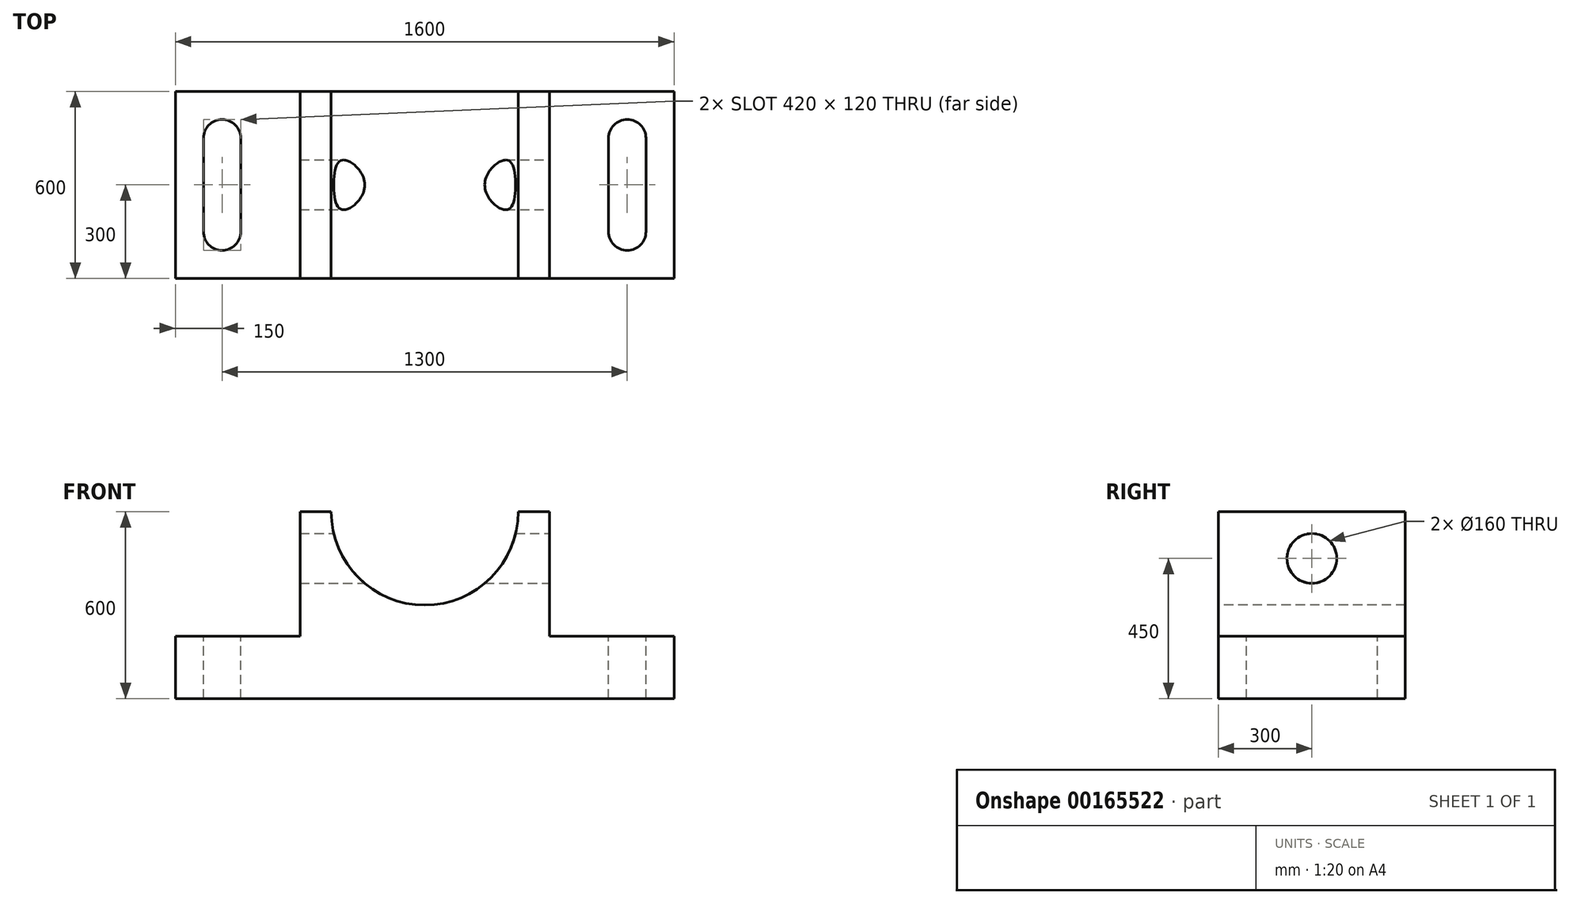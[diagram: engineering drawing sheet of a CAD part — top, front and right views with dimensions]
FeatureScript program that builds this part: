
annotation { "Feature Type Name" : "Feature", "Feature Type Description" : "" }
export const myFeature = defineFeature(function(context is Context, id is Id, definition is map)
    precondition{}
    {
        {
            var Q0;
            Q0=qCreatedBy(makeId("Front.planeOp"),FACE);
            var sketch = newSketch(context, id + "F0", { "sketchPlane" : qUnion([Q0])});
            skLineSegment(sketch, "E0.bottom", {"start": v(800, -300) * mm, "end": v(-800, -300) * mm});
            skLineSegment(sketch, "E0.top", {"start": v(800, 300) * mm, "end": v(-800, 300) * mm});
            skLineSegment(sketch, "E0.left", {"start": v(800, -300) * mm, "end": v(800, 300) * mm});
            skLineSegment(sketch, "E0.right", {"start": v(-800, -300) * mm, "end": v(-800, 300) * mm});
            skPoint(sketch, "E0.middle", {"position": v(0, 0) * mm});
            skSolve(sketch);
        }
        {
            var Q0;
            Q0 = qSketchRegion(id + "F0", true);
            extrude(context, id + "F1", {"entities" : qUnion([Q0]), "endBound" : BoundingType.SYMMETRIC, "depth" : 600 * mm});
        }
        {
            var Q0;
            Q0=makeQuery(id+"F1.opExtrude","CAP_FACE",FACE,{"disambiguationData":[OSD([sQuery(id+"F0.wireOp",EDGE,"E0.bottom"),sQuery(id+"F0.wireOp",EDGE,"E0.top"),sQuery(id+"F0.wireOp",EDGE,"E0.left"),sQuery(id+"F0.wireOp",EDGE,"E0.right")])],"isStart":false});
            var sketch = newSketch(context, id + "F2", { "sketchPlane" : qUnion([Q0])});
            skCircle(sketch, "E1", {"center": v(0, 300) * mm, "radius": 300 * mm});
            skSolve(sketch);
        }
        {
            var Q0;
            Q0 = qSketchRegion(id + "F2", true);
            extrude(context, id + "F3", {"entities" : qUnion([Q0]), "operationType" : NewBodyOperationType.REMOVE, "oppositeDirection" : true, "depth" : 600 * mm});
        }
        {
            var Q0;
            Q0=makeQuery(id+"F1.opExtrude","CAP_FACE",FACE,{"disambiguationData":[OSD([sQuery(id+"F0.wireOp",EDGE,"E0.bottom"),sQuery(id+"F0.wireOp",EDGE,"E0.top"),sQuery(id+"F0.wireOp",EDGE,"E0.left"),sQuery(id+"F0.wireOp",EDGE,"E0.right")])],"isStart":false});
            var sketch = newSketch(context, id + "F4", { "sketchPlane" : qUnion([Q0])});
            skLineSegment(sketch, "E2.bottom", {"start": v(-800, 300) * mm, "end": v(-400, 300) * mm});
            skLineSegment(sketch, "E2.top", {"start": v(-800, -100) * mm, "end": v(-400, -100) * mm});
            skLineSegment(sketch, "E2.left", {"start": v(-800, 300) * mm, "end": v(-800, -100) * mm});
            skLineSegment(sketch, "E2.right", {"start": v(-400, 300) * mm, "end": v(-400, -100) * mm});
            skLineSegment(sketch, "E3.bottom", {"start": v(800, 300) * mm, "end": v(400, 300) * mm});
            skLineSegment(sketch, "E3.top", {"start": v(800, -100) * mm, "end": v(400, -100) * mm});
            skLineSegment(sketch, "E3.left", {"start": v(800, 300) * mm, "end": v(800, -100) * mm});
            skLineSegment(sketch, "E3.right", {"start": v(400, 300) * mm, "end": v(400, -100) * mm});
            skSolve(sketch);
        }
        {
            var Q0;
            Q0 = qSketchRegion(id + "F4", true);
            extrude(context, id + "F5", {"entities" : qUnion([Q0]), "operationType" : NewBodyOperationType.REMOVE, "endBound" : BoundingType.THROUGH_ALL, "oppositeDirection" : true, "depth" : 25 * mm});
        }
        {
            var Q0;
            Q0=makeQuery(id+"F5.boolean.opBoolean","COPY",FACE,{"derivedFrom":makeQuery(id+"F5.opExtrude","SWEPT_FACE",FACE,{"disambiguationData":[OSD([sQuery(id+"F4.wireOp",EDGE,"E3.top")])]})});
            var sketch = newSketch(context, id + "F6", { "sketchPlane" : qUnion([Q0])});
            skLineSegment(sketch, "E4.bottom", {"start": v(710, -150) * mm, "end": v(590, -150) * mm});
            skLineSegment(sketch, "E4.top", {"start": v(710, 150) * mm, "end": v(590, 150) * mm});
            skLineSegment(sketch, "E4.left", {"start": v(710, -150) * mm, "end": v(710, 150) * mm});
            skLineSegment(sketch, "E4.right", {"start": v(590, -150) * mm, "end": v(590, 150) * mm});
            skPoint(sketch, "E4.middle", {"position": v(650, 0) * mm});
            skCircle(sketch, "E5", {"center": v(650, 150) * mm, "radius": 60 * mm});
            skCircle(sketch, "E6", {"center": v(650, -150) * mm, "radius": 60 * mm});
            skLineSegment(sketch, "E7.bottom", {"start": v(-590, -150) * mm, "end": v(-710, -150) * mm});
            skLineSegment(sketch, "E7.top", {"start": v(-590, 150) * mm, "end": v(-710, 150) * mm});
            skLineSegment(sketch, "E7.left", {"start": v(-590, -150) * mm, "end": v(-590, 150) * mm});
            skLineSegment(sketch, "E7.right", {"start": v(-710, -150) * mm, "end": v(-710, 150) * mm});
            skPoint(sketch, "E7.middle", {"position": v(-650, 0) * mm});
            skCircle(sketch, "E8", {"center": v(-650, 150) * mm, "radius": 60 * mm});
            skCircle(sketch, "E9", {"center": v(-650, -150) * mm, "radius": 60 * mm});
            skSolve(sketch);
        }
        {
            var Q0;
            Q0 = qSketchRegion(id + "F6", true);
            extrude(context, id + "F7", {"entities" : qUnion([Q0]), "operationType" : NewBodyOperationType.REMOVE, "endBound" : BoundingType.THROUGH_ALL, "oppositeDirection" : true, "depth" : 25 * mm});
        }
        {
            var Q0;
            Q0=makeQuery(id+"F5.boolean.opBoolean","COPY",FACE,{"derivedFrom":makeQuery(id+"F5.opExtrude","SWEPT_FACE",FACE,{"disambiguationData":[OSD([sQuery(id+"F4.wireOp",EDGE,"E3.right")])]})});
            var sketch = newSketch(context, id + "F8", { "sketchPlane" : qUnion([Q0])});
            skCircle(sketch, "E10", {"center": v(0, 150) * mm, "radius": 80 * mm});
            skPoint(sketch, "E10.centerSnap0", {"position": v(0, 300) * mm});
            skSolve(sketch);
        }
        {
            var Q0;
            Q0 = qSketchRegion(id + "F8", true);
            extrude(context, id + "F9", {"entities" : qUnion([Q0]), "operationType" : NewBodyOperationType.REMOVE, "endBound" : BoundingType.THROUGH_ALL, "oppositeDirection" : true, "depth" : 25 * mm});
        }
    });
